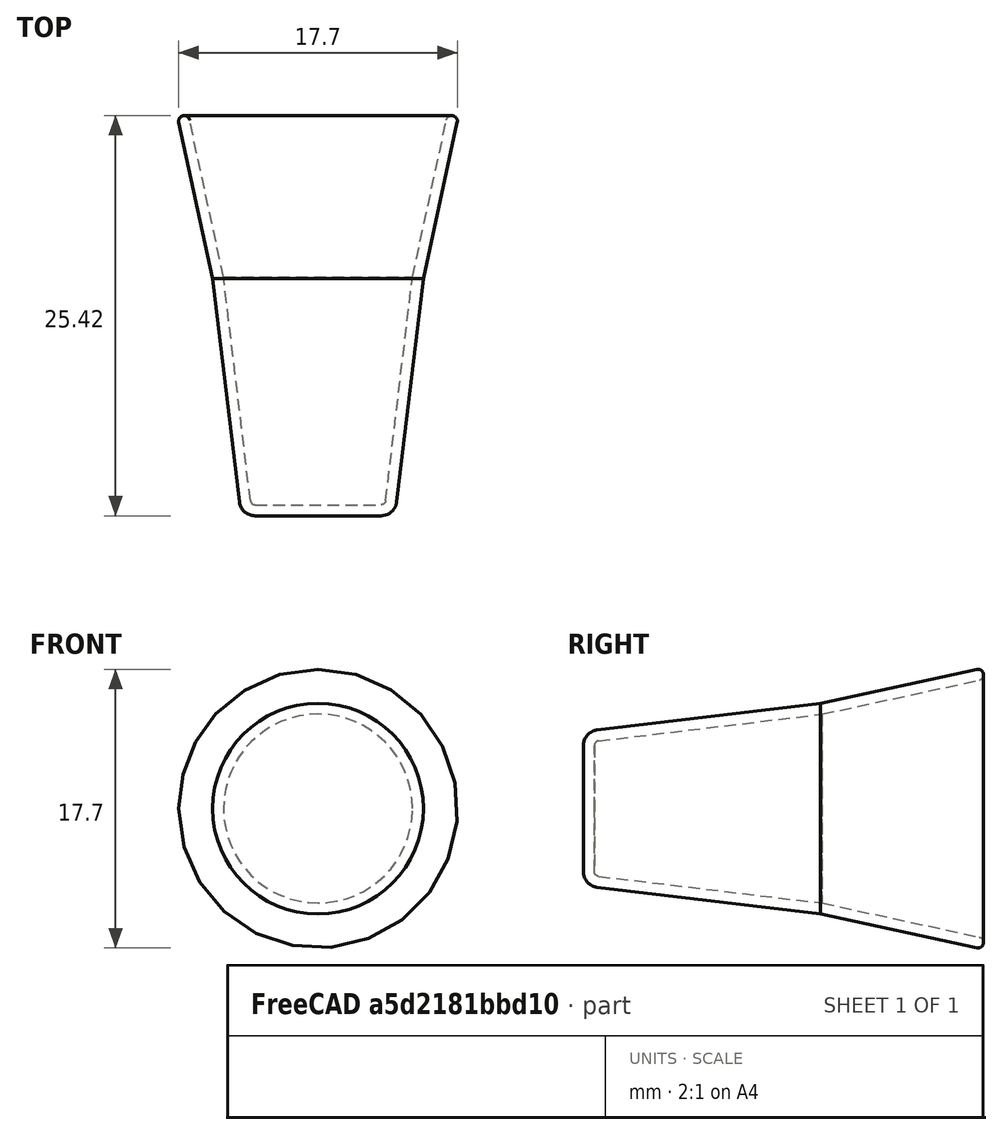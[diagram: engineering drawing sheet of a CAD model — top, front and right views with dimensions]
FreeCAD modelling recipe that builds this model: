
FCSTD DOCUMENT  (FreeCAD 0.16R6712 (Git))
Label: cup
License: All rights reserved
LicenseURL: http://en.wikipedia.org/wiki/All_rights_reserved
objects: Sketcher::SketchObject×1, PartDesign::Revolution×1, Mesh::Feature×1
note: 3 computed .brp shape members not serialized (recipe doc carries the construction recipe); baked Part::Feature solids carry a one-line shape summary decoded from their .brp

FEATURE [Sketcher::SketchObject] Sketch
  sketch-geometry (10):
    g0: LineSegment StartX=0 StartY=0 StartZ=0 EndX=-4 EndY=0 EndZ=0
    g1: LineSegment StartX=-4.9929 StartY=0.881055 StartZ=0 EndX=-6.69112 EndY=15.057 EndZ=0
    g2: ArcOfCircle CenterX=-8.5 CenterY=25.0681 CenterZ=0 NormalX=0 NormalY=0 NormalZ=1 Radius=0.35 StartAngle=0.21318 EndAngle=3.35474
    g3: LineSegment StartX=-4 StartY=0.7 StartZ=0 EndX=0 EndY=0.7 EndZ=0
    g4: LineSegment StartX=0 StartY=0.7 StartZ=0 EndX=0 EndY=0 EndZ=0
    g5: ArcOfCircle CenterX=-4 CenterY=1 CenterZ=0 NormalX=0 NormalY=0 NormalZ=1 Radius=0.3 StartAngle=3.26082 EndAngle=4.71239
    g6: ArcOfCircle CenterX=-4 CenterY=1 CenterZ=0 NormalX=0 NormalY=0 NormalZ=1 Radius=1 StartAngle=3.26082 EndAngle=4.71239
    g7: LineSegment StartX=-4.29787 StartY=0.964317 StartZ=0 EndX=-6 EndY=15.173 EndZ=0
    g8: LineSegment StartX=-6 StartY=15.173 StartZ=0 EndX=-8.15792 EndY=25.1421 EndZ=0
    g9: LineSegment StartX=-8.84208 StartY=24.994 StartZ=0 EndX=-6.69112 EndY=15.057 EndZ=0
  constraints (26):
    c: Coincident(g0,g-1)
    c: Horizontal(g3)
    c: Coincident(g4,g3)
    c: Coincident(g4,g-1)
    c: DistanceY(g-1,g3) = 0.7
    c: Tangent(g3,g5) = -1.5708
    c: Tangent(g0,g6) = 1.5708
    c: Tangent(g1,g6) = 1.5708
    c: Radius(g6) = 1
    c: PointOnObject(g0,g-1)
    c: Vertical(g4)
    c: DistanceX(g-2,g5) = -4
    c: Radius(g2) = 0.35
    c: Coincident(g7,g5)
    c: Parallel(g1,g7)
    c: Coincident(g8,g7)
    c: Tangent(g5,g7)
    c: Coincident(g5,g6)
    c: Coincident(g9,g1)
    c: Parallel(g8,g9)
    c: Coincident(g8,g2)
    c: Tangent(g8,g2)
    c: Coincident(g2,g9)
    c: Tangent(g2,g9)
    c: DistanceX(g-2,g7) = -6
    c: DistanceX(g-2,g2) = -8.5
FEATURE [PartDesign::Revolution] Revolution
  Angle = 360
  Axis = (0,1,0)
  Base = (0,0,0)
  ReferenceAxis = -> Sketch [V_Axis]
  Sketch = -> Sketch
FEATURE [Mesh::Feature] Mesh  label="Revolution (Meshed)"
